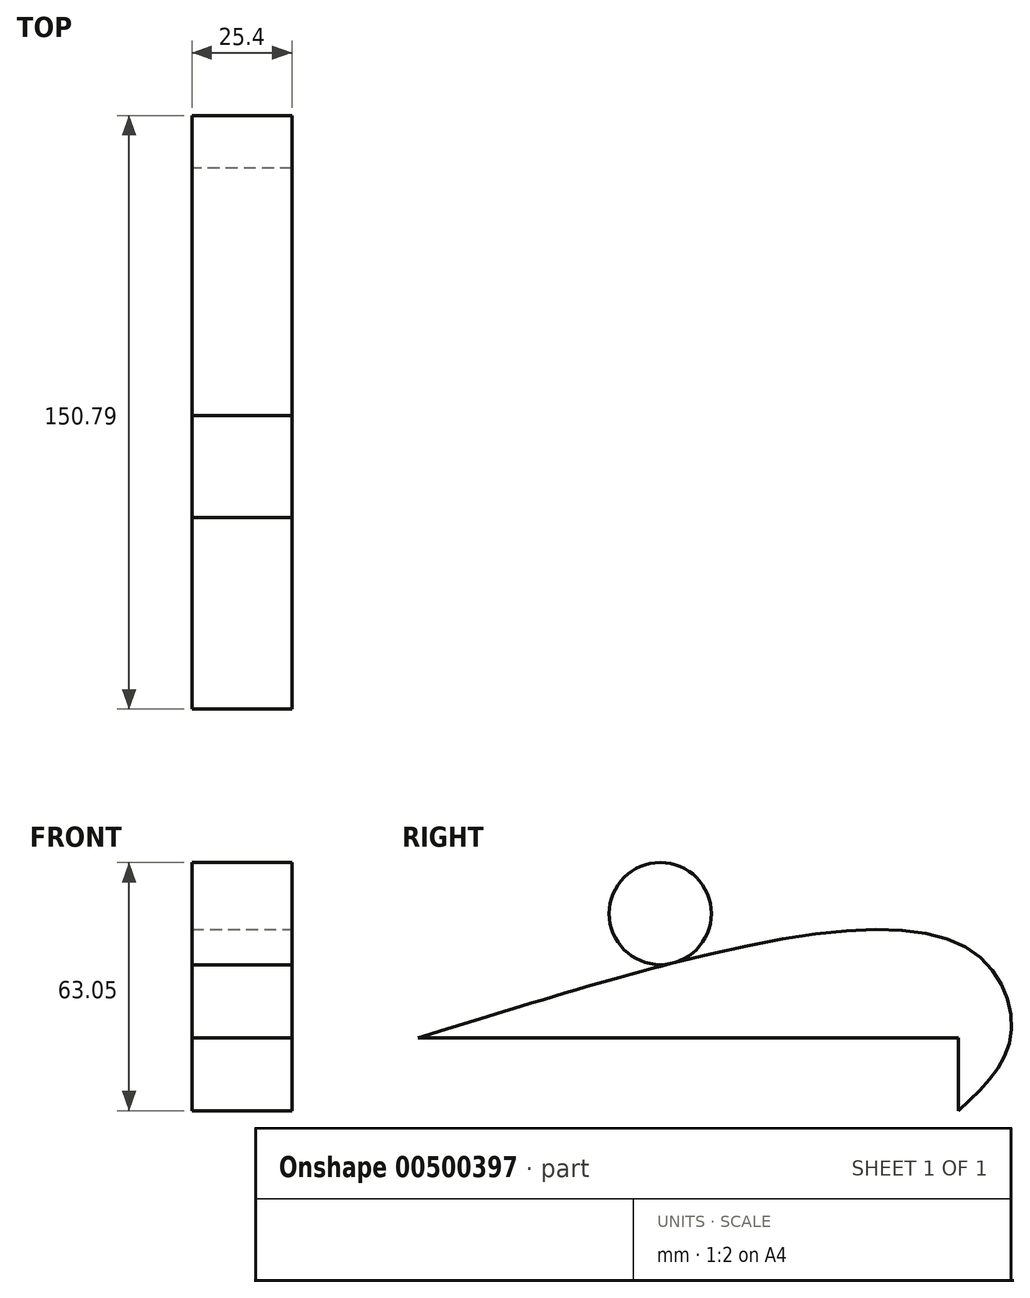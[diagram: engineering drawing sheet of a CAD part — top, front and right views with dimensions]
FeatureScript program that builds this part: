
annotation { "Feature Type Name" : "Feature", "Feature Type Description" : "" }
export const myFeature = defineFeature(function(context is Context, id is Id, definition is map)
    precondition{}
    {
        {
            var Q0;
            Q0=qCreatedBy(makeId("Right.planeOp"),FACE);
            var sketch = newSketch(context, id + "F0", { "sketchPlane" : qUnion([Q0])});
            skLineSegment(sketch, "E0.bottom", {"start": v(0, 0) * mm, "end": v(-137.36, 0) * mm});
            skLineSegment(sketch, "E0.top", {"start": v(0, -18.45) * mm, "end": v(-137.36, -18.45) * mm});
            skLineSegment(sketch, "E0.left", {"start": v(0, 0) * mm, "end": v(0, -18.45) * mm});
            skLineSegment(sketch, "E0.right", {"start": v(-137.36, 0) * mm, "end": v(-137.36, -18.45) * mm});
            skFitSpline(sketch, "E1", {"points": [v(-137.36, 0) * mm, v(0, 24.03) * mm, v(13.14, 0) * mm, v(0, -18.45) * mm], "startDerivative": vector(314.52, 97.97) * mm, "endDerivative": vector(-81.15, -75.15) * mm});
            skCircle(sketch, "E2", {"center": v(-75.8, 31.62) * mm, "radius": 12.98 * mm});
            skSolve(sketch);
        }
        {
            var Q0;
            Q0=makeQuery(id+"F0.imprint","IMPRINT",FACE,{"disambiguationData":[TD([[makeQuery(id+"F0.imprint","IMPRINT",EDGE,{"derivedFrom":sQuery(id+"F0.wireOp",EDGE,"E2")}),1.0]])]});
            var Q1;
            {var subQ0=sQuery(id+"F0.wireOp",EDGE,"E0.bottom");Q1=makeQuery(id+"F0.imprint","IMPRINT",FACE,{"disambiguationData":[TD([[makeQuery(id+"F0.imprint","IMPRINT",EDGE,{"derivedFrom":subQ0}),-1.0]])]});}
            extrude(context, id + "F1", {"entities" : qUnion([Q0, Q1]), "depth" : 25.4 * mm});
        }
    });
